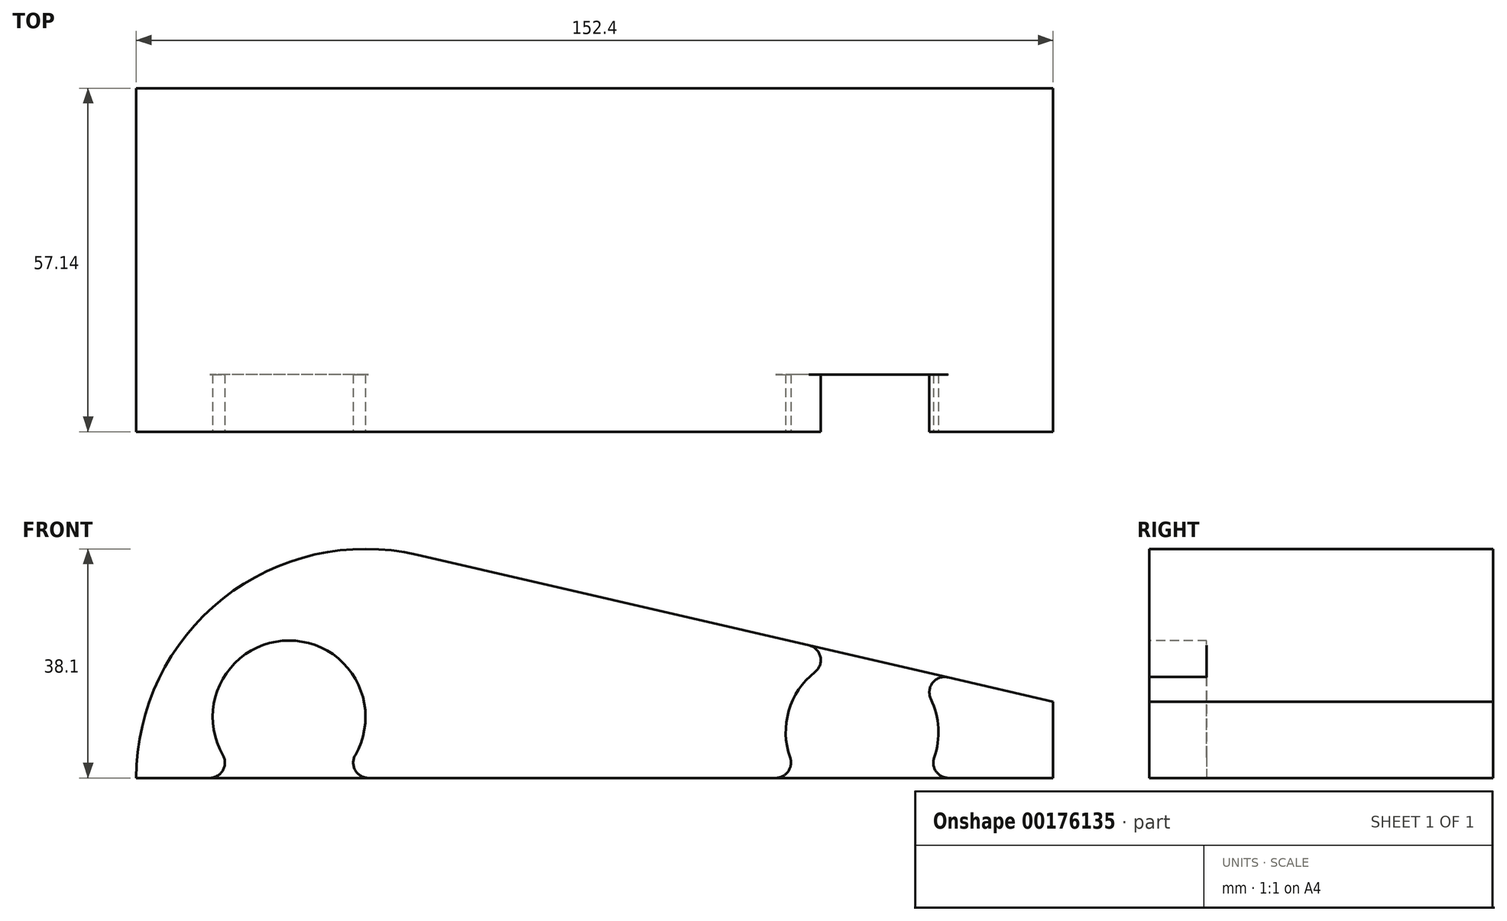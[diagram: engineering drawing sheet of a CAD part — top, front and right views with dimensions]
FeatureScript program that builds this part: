
annotation { "Feature Type Name" : "Feature", "Feature Type Description" : "" }
export const myFeature = defineFeature(function(context is Context, id is Id, definition is map)
    precondition{}
    {
        {
            var Q0;
            Q0=qCreatedBy(makeId("Front.planeOp"),FACE);
            var sketch = newSketch(context, id + "F0", { "sketchPlane" : qUnion([Q0])});
            skLineSegment(sketch, "E0", {"start": v(0, 0) * mm, "end": v(-152.4, 0) * mm});
            skLineSegment(sketch, "E1", {"start": v(0, 0) * mm, "end": v(0, 12.7) * mm});
            skArc(sketch, "E2", {"start": v(-105.72, 37.12) * mm, "mid": v(-138.02, 29.82) * mm, "end": v(-152.4, 0) * mm});
            skLineSegment(sketch, "E3", {"start": v(-152.4, 38.1) * mm, "end": v(-152.4, 0) * mm, "construction": true});
            skLineSegment(sketch, "E4", {"start": v(-105.72, 37.12) * mm, "end": v(0, 12.7) * mm});
            skLineSegment(sketch, "E5", {"start": v(-152.4, 38.1) * mm, "end": v(-83.26, 38.1) * mm, "construction": true});
            skSolve(sketch);
        }
        {
            var Q0;
            Q0 = qSketchRegion(id + "F0", true);
            extrude(context, id + "F1", {"entities" : qUnion([Q0]), "endBound" : BoundingType.SYMMETRIC, "depth" : 57.15 * mm});
        }
        {
            var Q0;
            Q0=makeQuery(id+"F1.opExtrude","CAP_FACE",FACE,{"disambiguationData":[OSD([sQuery(id+"F0.wireOp",EDGE,"E0"),sQuery(id+"F0.wireOp",EDGE,"4b855ea8-11fb-456d-b135-d976b07b8fe8"),sQuery(id+"F0.wireOp",EDGE,"E1"),sQuery(id+"F0.wireOp",EDGE,"G8eNXFR9-HTIZ-Whdn-xpxj-u5TztKd5zlmO")])],"isStart":false});
            var sketch = newSketch(context, id + "F2", { "sketchPlane" : qUnion([Q0])});
            skCircle(sketch, "E6", {"center": v(-127, 10.16) * mm, "radius": 12.7 * mm});
            skCircle(sketch, "E7", {"center": v(-31.75, 7.62) * mm, "radius": 12.7 * mm});
            skLineSegment(sketch, "E8", {"start": v(-161.18, -1.63) * mm, "end": v(0, -5.93) * mm, "construction": true});
            skSolve(sketch);
        }
        {
            var Q0;
            Q0 = qSketchRegion(id + "F2", true);
            var Q1;
            Q1=sQuery(id+"F2.wireOp",EDGE,"E8");
            extrude(context, id + "F3", {"entities" : qUnion([Q0]), "operationType" : NewBodyOperationType.REMOVE, "surfaceEntities" : qUnion([Q1]), "oppositeDirection" : true, "depth" : 9.52 * mm});
        }
        {
            var Q0;
            Q0=makeQuery(id+"F3.boolean.opBoolean","INTERSECT",EDGE,{"disambiguationData":[OD(1.0)],"derivedFrom":[makeQuery(id+"F1.opExtrude","SWEPT_FACE",FACE,{"disambiguationData":[OSD([sQuery(id+"F0.wireOp",EDGE,"E4")])]}),makeQuery(id+"F3.opExtrude","SWEPT_FACE",FACE,{"disambiguationData":[OSD([sQuery(id+"F2.wireOp",EDGE,"E7")])]})]});
            var Q1;
            Q1=makeQuery(id+"F3.boolean.opBoolean","INTERSECT",EDGE,{"disambiguationData":[OD(0.0)],"derivedFrom":[makeQuery(id+"F1.opExtrude","SWEPT_FACE",FACE,{"disambiguationData":[OSD([sQuery(id+"F0.wireOp",EDGE,"E4")])]}),makeQuery(id+"F3.opExtrude","SWEPT_FACE",FACE,{"disambiguationData":[OSD([sQuery(id+"F2.wireOp",EDGE,"E7")])]})]});
            var Q2;
            Q2=makeQuery(id+"F3.boolean.opBoolean","INTERSECT",EDGE,{"disambiguationData":[OD(1.0)],"derivedFrom":[makeQuery(id+"F1.opExtrude","SWEPT_FACE",FACE,{"disambiguationData":[OSD([sQuery(id+"F0.wireOp",EDGE,"E0")])]}),makeQuery(id+"F3.opExtrude","SWEPT_FACE",FACE,{"disambiguationData":[OSD([sQuery(id+"F2.wireOp",EDGE,"E7")])]})]});
            var Q3;
            Q3=makeQuery(id+"F3.boolean.opBoolean","INTERSECT",EDGE,{"disambiguationData":[OD(0.0)],"derivedFrom":[makeQuery(id+"F1.opExtrude","SWEPT_FACE",FACE,{"disambiguationData":[OSD([sQuery(id+"F0.wireOp",EDGE,"E0")])]}),makeQuery(id+"F3.opExtrude","SWEPT_FACE",FACE,{"disambiguationData":[OSD([sQuery(id+"F2.wireOp",EDGE,"E7")])]})]});
            var Q4;
            Q4=makeQuery(id+"F3.boolean.opBoolean","INTERSECT",EDGE,{"disambiguationData":[OD(1.0)],"derivedFrom":[makeQuery(id+"F1.opExtrude","SWEPT_FACE",FACE,{"disambiguationData":[OSD([sQuery(id+"F0.wireOp",EDGE,"E0")])]}),makeQuery(id+"F3.opExtrude","SWEPT_FACE",FACE,{"disambiguationData":[OSD([sQuery(id+"F2.wireOp",EDGE,"E6")])]})]});
            var Q5;
            Q5=makeQuery(id+"F3.boolean.opBoolean","INTERSECT",EDGE,{"disambiguationData":[OD(0.0)],"derivedFrom":[makeQuery(id+"F1.opExtrude","SWEPT_FACE",FACE,{"disambiguationData":[OSD([sQuery(id+"F0.wireOp",EDGE,"E0")])]}),makeQuery(id+"F3.opExtrude","SWEPT_FACE",FACE,{"disambiguationData":[OSD([sQuery(id+"F2.wireOp",EDGE,"E6")])]})]});
            var Q6;
            Q6=makeQuery(id+"FjUL6NBNlzsGPx0_1.1.F3.boolean.opBoolean","INTERSECT",EDGE,{"disambiguationData":[OD(0.0)],"derivedFrom":[makeQuery(id+"F1.opExtrude","SWEPT_FACE",FACE,{"disambiguationData":[OSD([sQuery(id+"F0.wireOp",EDGE,"E0")])]}),makeQuery(id+"FjUL6NBNlzsGPx0_1.1.F3.opExtrude","SWEPT_FACE",FACE,{"disambiguationData":[OSD([sQuery(id+"F2.wireOp",EDGE,"E7")])]})]});
            var Q7;
            Q7=makeQuery(id+"FjUL6NBNlzsGPx0_1.1.F3.boolean.opBoolean","INTERSECT",EDGE,{"disambiguationData":[OD(0.0)],"derivedFrom":[makeQuery(id+"F1.opExtrude","SWEPT_FACE",FACE,{"disambiguationData":[OSD([sQuery(id+"F0.wireOp",EDGE,"E4")])]}),makeQuery(id+"FjUL6NBNlzsGPx0_1.1.F3.opExtrude","SWEPT_FACE",FACE,{"disambiguationData":[OSD([sQuery(id+"F2.wireOp",EDGE,"E7")])]})]});
            var Q8;
            Q8=makeQuery(id+"FjUL6NBNlzsGPx0_1.1.F3.boolean.opBoolean","INTERSECT",EDGE,{"disambiguationData":[OD(1.0)],"derivedFrom":[makeQuery(id+"F1.opExtrude","SWEPT_FACE",FACE,{"disambiguationData":[OSD([sQuery(id+"F0.wireOp",EDGE,"E0")])]}),makeQuery(id+"FjUL6NBNlzsGPx0_1.1.F3.opExtrude","SWEPT_FACE",FACE,{"disambiguationData":[OSD([sQuery(id+"F2.wireOp",EDGE,"E6")])]})]});
            var Q9;
            Q9=makeQuery(id+"FjUL6NBNlzsGPx0_1.1.F3.boolean.opBoolean","INTERSECT",EDGE,{"disambiguationData":[OD(1.0)],"derivedFrom":[makeQuery(id+"F1.opExtrude","SWEPT_FACE",FACE,{"disambiguationData":[OSD([sQuery(id+"F0.wireOp",EDGE,"E4")])]}),makeQuery(id+"FjUL6NBNlzsGPx0_1.1.F3.opExtrude","SWEPT_FACE",FACE,{"disambiguationData":[OSD([sQuery(id+"F2.wireOp",EDGE,"E7")])]})]});
            var Q10;
            Q10=makeQuery(id+"FjUL6NBNlzsGPx0_1.1.F3.boolean.opBoolean","INTERSECT",EDGE,{"disambiguationData":[OD(1.0)],"derivedFrom":[makeQuery(id+"F1.opExtrude","SWEPT_FACE",FACE,{"disambiguationData":[OSD([sQuery(id+"F0.wireOp",EDGE,"E0")])]}),makeQuery(id+"FjUL6NBNlzsGPx0_1.1.F3.opExtrude","SWEPT_FACE",FACE,{"disambiguationData":[OSD([sQuery(id+"F2.wireOp",EDGE,"E7")])]})]});
            var Q11;
            Q11=makeQuery(id+"FjUL6NBNlzsGPx0_1.1.F3.boolean.opBoolean","INTERSECT",EDGE,{"disambiguationData":[OD(0.0)],"derivedFrom":[makeQuery(id+"F1.opExtrude","SWEPT_FACE",FACE,{"disambiguationData":[OSD([sQuery(id+"F0.wireOp",EDGE,"E0")])]}),makeQuery(id+"FjUL6NBNlzsGPx0_1.1.F3.opExtrude","SWEPT_FACE",FACE,{"disambiguationData":[OSD([sQuery(id+"F2.wireOp",EDGE,"E6")])]})]});
            fillet(context, id + "F4", {"entities" : qUnion([Q0, Q1, Q2, Q3, Q4, Q5, Q6, Q7, Q8, Q9, Q10, Q11]), "radius" : 2.54 * mm, "tangentPropagation" : true, "allowEdgeOverflow" : false});
        }
    });
